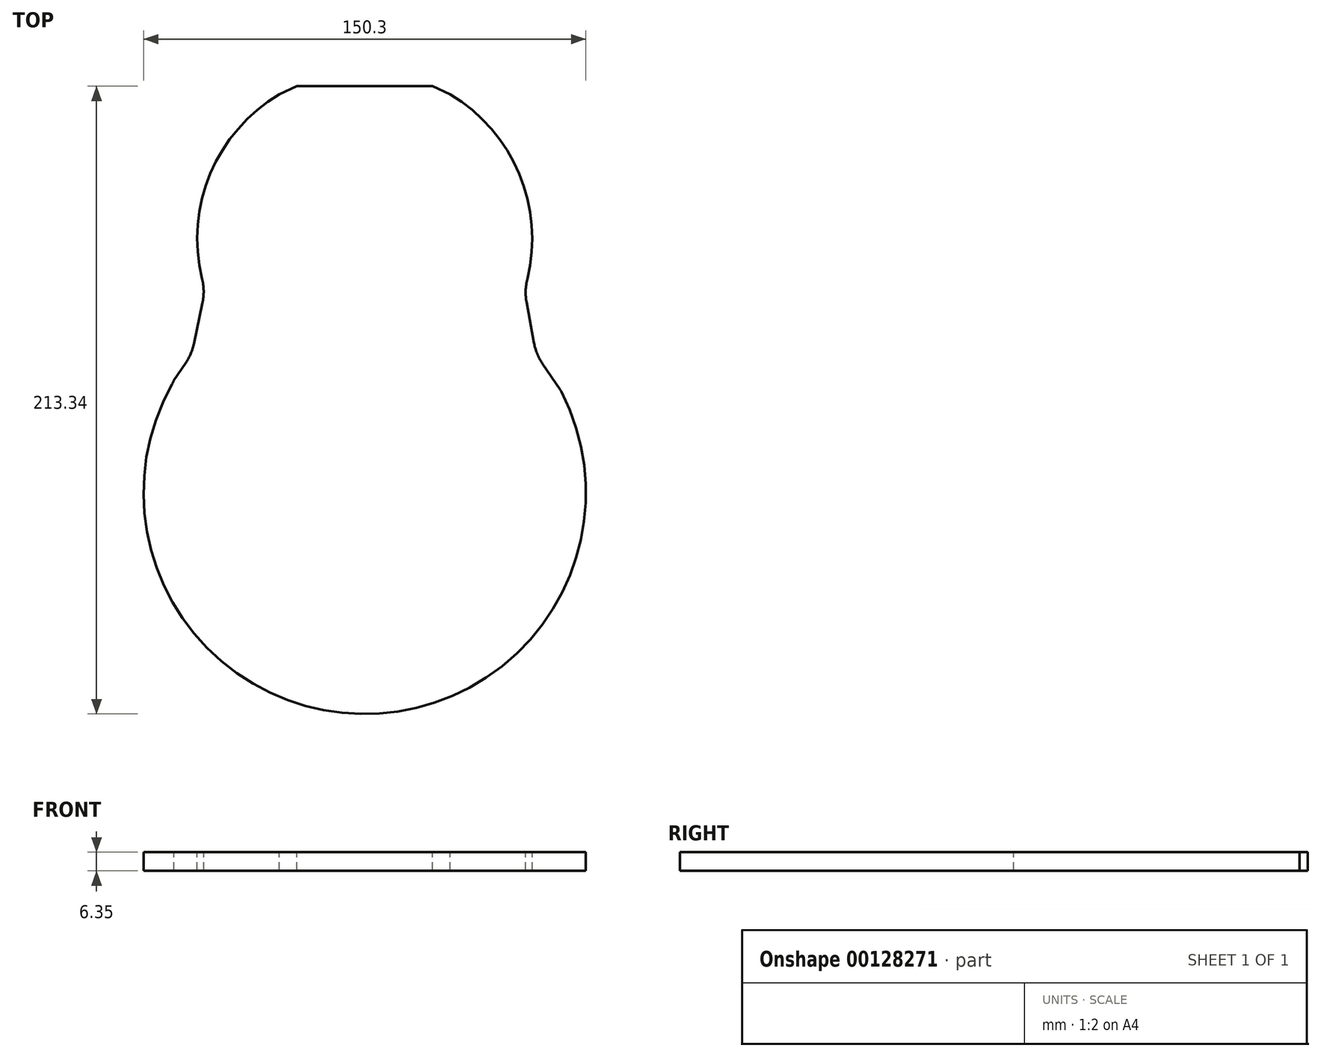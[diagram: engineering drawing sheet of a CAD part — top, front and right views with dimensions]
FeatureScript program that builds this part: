
annotation { "Feature Type Name" : "Feature", "Feature Type Description" : "" }
export const myFeature = defineFeature(function(context is Context, id is Id, definition is map)
    precondition{}
    {
        {
            var Q0;
            Q0=qCreatedBy(makeId("Top.planeOp"),FACE);
            var sketch = newSketch(context, id + "F0", { "sketchPlane" : qUnion([Q0])});
            skArc(sketch, "E0", {"start": v(-71.1, 39.83) * mm, "mid": v(-1.08, -81.5) * mm, "end": v(72.13, 37.93) * mm});
            skPoint(sketch, "E1.visualSharp", {"position": v(-70.75, 40.46) * mm});
            skArc(sketch, "E1.filletArc", {"start": v(-71.1, 39.83) * mm, "mid": v(-70.78, 40.49) * mm, "end": v(-70.54, 41.17) * mm});
            skPoint(sketch, "E2.center.orphan", {"position": v(0, 86.45) * mm});
            skLineSegment(sketch, "E3", {"start": v(72.13, 37.93) * mm, "end": v(64.18, 49.7) * mm});
            skLineSegment(sketch, "E4", {"start": v(-64.73, 49.7) * mm, "end": v(-70.54, 41.17) * mm});
            skArc(sketch, "E5", {"start": v(60.72, 68.63) * mm, "mid": v(58.81, 109.8) * mm, "end": v(31.95, 141.07) * mm});
            skLineSegment(sketch, "E6", {"start": v(64.18, 49.7) * mm, "end": v(60.72, 68.63) * mm});
            skLineSegment(sketch, "E7", {"start": v(-60.74, 68.69) * mm, "end": v(-64.73, 49.7) * mm});
            skPoint(sketch, "E8.orphan", {"position": v(0, 144.54) * mm});
            skPoint(sketch, "E9.orphan", {"position": v(-24.5, 144.54) * mm});
            skPoint(sketch, "E10.start.orphan", {"position": v(24.5, 144.54) * mm});
            skArc(sketch, "E11.trimOffspring", {"start": v(-31.95, 141.07) * mm, "mid": v(-58.8, 109.83) * mm, "end": v(-60.74, 68.69) * mm});
            skLineSegment(sketch, "E12", {"start": v(0, 141.07) * mm, "end": v(0, 144.54) * mm});
            skPoint(sketch, "E12.endSnap0", {"position": v(0, 141.07) * mm});
            skLineSegment(sketch, "E13", {"start": v(0, 144.54) * mm, "end": v(24.5, 144.54) * mm});
            skLineSegment(sketch, "E14", {"start": v(0, 144.54) * mm, "end": v(-24.5, 144.54) * mm});
            skLineSegment(sketch, "E15", {"start": v(31.95, 141.07) * mm, "end": v(24.5, 144.54) * mm});
            skLineSegment(sketch, "E16", {"start": v(-24.5, 144.54) * mm, "end": v(-31.95, 141.07) * mm});
            skSolve(sketch);
        }
        {
            var Q0;
            {var subQ0=sQuery(id+"F0.wireOp",EDGE,"E1.filletArc");Q0=makeQuery(id+"F0.imprint","IMPRINT",FACE,{"disambiguationData":[TD([[makeQuery(id+"F0.imprint","IMPRINT",EDGE,{"derivedFrom":subQ0}),-1.0]])]});}
            extrude(context, id + "F1", {"entities" : qUnion([Q0]), "depth" : 6.35 * mm});
        }
        {
            var Q0;
            Q0=makeQuery(id+"F1.opExtrude","SWEPT_EDGE",EDGE,{"disambiguationData":[OSD([sQuery(id+"F0.wireOp",EDGE,"E5"),sQuery(id+"F0.wireOp",EDGE,"E6")])]});
            var Q1;
            Q1=makeQuery(id+"F1.opExtrude","SWEPT_EDGE",EDGE,{"disambiguationData":[OSD([sQuery(id+"F0.wireOp",EDGE,"E0"),sQuery(id+"F0.wireOp",EDGE,"E3")])]});
            var Q2;
            Q2=makeQuery(id+"F1.opExtrude","SWEPT_EDGE",EDGE,{"disambiguationData":[OSD([sQuery(id+"F0.wireOp",EDGE,"E3"),sQuery(id+"F0.wireOp",EDGE,"E6")])]});
            var Q3;
            Q3=makeQuery(id+"F1.opExtrude","SWEPT_EDGE",EDGE,{"disambiguationData":[OSD([sQuery(id+"F0.wireOp",EDGE,"E4"),sQuery(id+"F0.wireOp",EDGE,"E7")])]});
            var Q4;
            Q4=makeQuery(id+"F1.opExtrude","SWEPT_EDGE",EDGE,{"disambiguationData":[OSD([sQuery(id+"F0.wireOp",EDGE,"E7"),sQuery(id+"F0.wireOp",EDGE,"E11.trimOffspring")])]});
            fillet(context, id + "F2", {"entities" : qUnion([Q0, Q1, Q2, Q3, Q4]), "radius" : 12.7 * mm, "tangentPropagation" : true, "allowEdgeOverflow" : false});
        }
        {
            var Q0;
            Q0=makeQuery(id+"F1.opExtrude","CAP_FACE",FACE,{"disambiguationData":[OSD([sQuery(id+"F0.wireOp",EDGE,"E0"),sQuery(id+"F0.wireOp",EDGE,"E1.filletArc"),sQuery(id+"F0.wireOp",EDGE,"E3"),sQuery(id+"F0.wireOp",EDGE,"E4"),sQuery(id+"F0.wireOp",EDGE,"E5"),sQuery(id+"F0.wireOp",EDGE,"E6"),sQuery(id+"F0.wireOp",EDGE,"E7"),sQuery(id+"F0.wireOp",EDGE,"E11.trimOffspring"),sQuery(id+"F0.wireOp",EDGE,"E13"),sQuery(id+"F0.wireOp",EDGE,"E14"),sQuery(id+"F0.wireOp",EDGE,"E15"),sQuery(id+"F0.wireOp",EDGE,"E16")])],"isStart":false});
            var sketch = newSketch(context, id + "F3", { "sketchPlane" : qUnion([Q0])});
            skLineSegment(sketch, "E17.0", {"start": v(-23.1, 138.19) * mm, "end": v(-29, 135.44) * mm});
            skLineSegment(sketch, "E17.1", {"start": v(-23.1, 138.19) * mm, "end": v(23.1, 138.19) * mm});
            skLineSegment(sketch, "E17.2", {"start": v(29, 135.44) * mm, "end": v(23.1, 138.19) * mm});
            skArc(sketch, "E17.3", {"start": v(55.24, 72.7) * mm, "mid": v(52.52, 108.41) * mm, "end": v(29, 135.44) * mm});
            skArc(sketch, "E17.4", {"start": v(54.99, 64.67) * mm, "mid": v(54.69, 68.7) * mm, "end": v(55.24, 72.7) * mm});
            skLineSegment(sketch, "E17.5", {"start": v(-60.9, 44.03) * mm, "end": v(-64.82, 38.29) * mm});
            skArc(sketch, "E17.6", {"start": v(-58, 50.85) * mm, "mid": v(-59.12, 47.3) * mm, "end": v(-60.9, 44.03) * mm});
            skLineSegment(sketch, "E17.7", {"start": v(-55.15, 64.42) * mm, "end": v(-58, 50.85) * mm});
            skArc(sketch, "E17.8", {"start": v(-55.29, 72.87) * mm, "mid": v(-54.74, 68.65) * mm, "end": v(-55.15, 64.42) * mm});
            skArc(sketch, "E17.9", {"start": v(-65.56, 36.73) * mm, "mid": v(-65.17, 37.5) * mm, "end": v(-64.82, 38.29) * mm});
            skArc(sketch, "E17.10", {"start": v(-65.56, 36.73) * mm, "mid": v(-1.36, -75.14) * mm, "end": v(66.85, 34.32) * mm});
            skArc(sketch, "E17.11", {"start": v(66.85, 34.32) * mm, "mid": v(66.67, 34.66) * mm, "end": v(66.46, 34.98) * mm});
            skLineSegment(sketch, "E17.12", {"start": v(66.46, 34.98) * mm, "end": v(60.41, 43.92) * mm});
            skArc(sketch, "E17.13", {"start": v(60.41, 43.92) * mm, "mid": v(58.56, 47.4) * mm, "end": v(57.45, 51.18) * mm});
            skArc(sketch, "E17.14", {"start": v(-29, 135.44) * mm, "mid": v(-52.48, 108.5) * mm, "end": v(-55.29, 72.87) * mm});
            skLineSegment(sketch, "E17.15", {"start": v(57.45, 51.18) * mm, "end": v(54.99, 64.67) * mm});
            skSolve(sketch);
        }
        {
            var Q0;
            Q0=makeQuery(id+"F3.imprint","IMPRINT",FACE,{"disambiguationData":[TD([[makeQuery(id+"F3.imprint","IMPRINT",EDGE,{"derivedFrom":sQuery(id+"F3.wireOp",EDGE,"kXYZUbgt-hvK8-WOMi-bS6y-uFz0kxA99WS2")}),1.0]])]});
            var Q1;
            Q1=makeQuery(id+"F3.imprint","IMPRINT",FACE,{"disambiguationData":[TD([[makeQuery(id+"F3.imprint","IMPRINT",EDGE,{"derivedFrom":sQuery(id+"F3.wireOp",EDGE,"E17.0")}),-1.0]])]});
            extrude(context, id + "F4", {"entities" : qUnion([Q0, Q1]), "operationType" : NewBodyOperationType.REMOVE, "endBound" : BoundingType.THROUGH_ALL, "oppositeDirection" : true, "depth" : 25.4 * mm});
        }
    });
